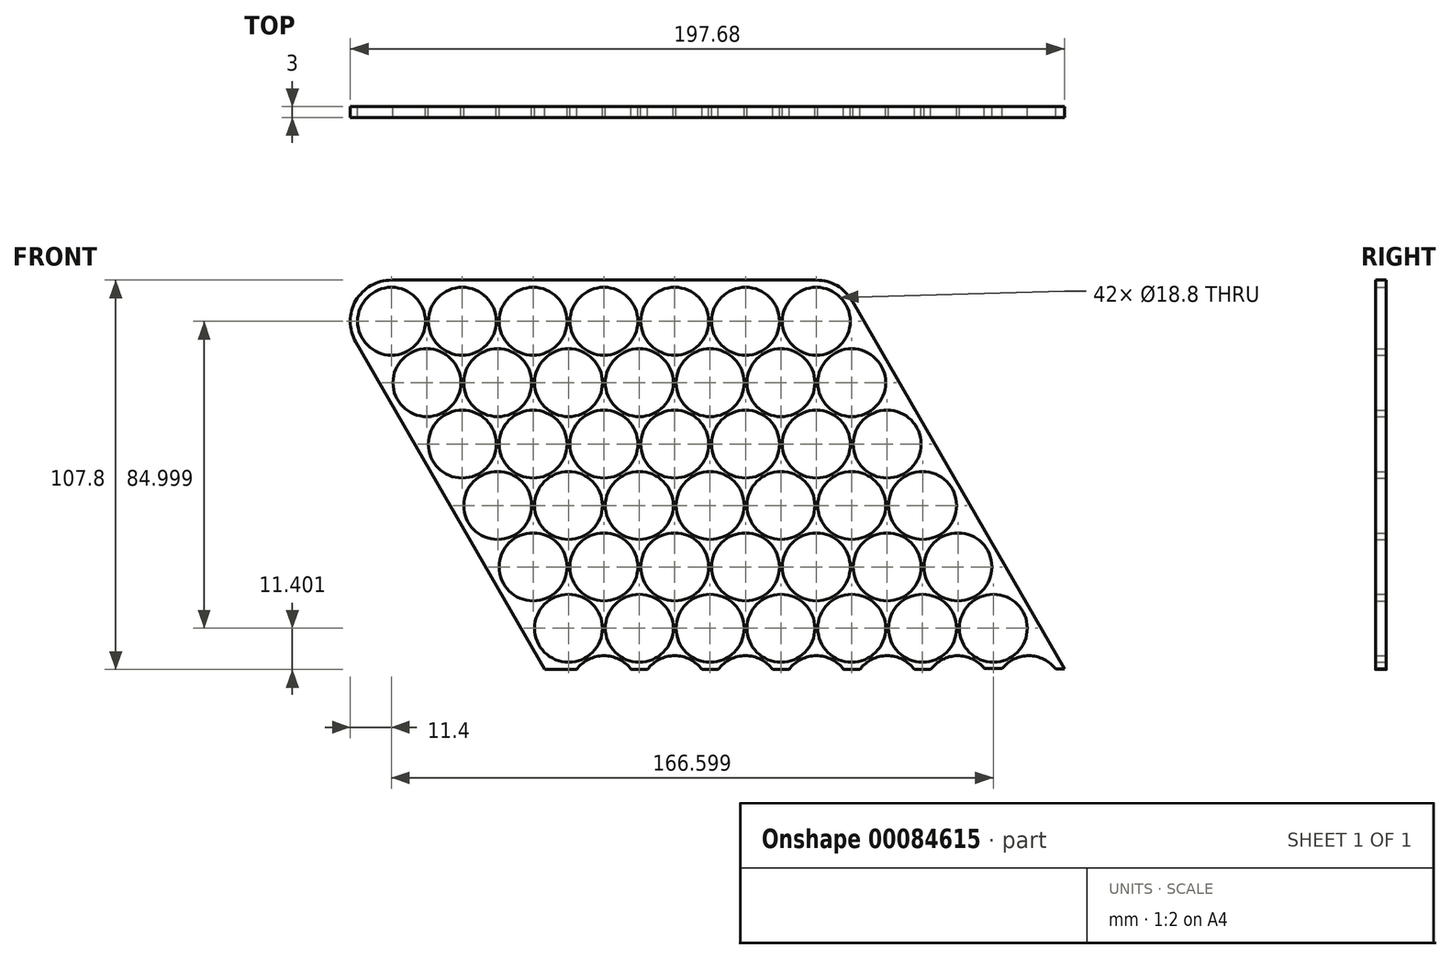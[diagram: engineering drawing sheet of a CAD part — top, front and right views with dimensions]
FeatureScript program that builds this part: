
annotation { "Feature Type Name" : "Feature", "Feature Type Description" : "" }
export const myFeature = defineFeature(function(context is Context, id is Id, definition is map)
    precondition{}
    {
        {
            var Q0;
            Q0=qCreatedBy(makeId("Front.planeOp"),FACE);
            var sketch = newSketch(context, id + "F0", { "sketchPlane" : qUnion([Q0]) });
            skCircle(sketch, "E0", {"center": v(0, 0) * mm, "radius": 9.4 * mm});
            skCircle(sketch, "E1.1.0.0", {"center": v(19.6, 0) * mm, "radius": 9.4 * mm});
            skCircle(sketch, "E1.2.0.0", {"center": v(39.2, 0) * mm, "radius": 9.4 * mm});
            skCircle(sketch, "E1.3.0.0", {"center": v(58.8, 0) * mm, "radius": 9.4 * mm});
            skLineSegment(sketch, "E1.direction1", {"start": v(0, 0) * mm, "end": v(19.6, 0) * mm, "construction": true});
            skLineSegment(sketch, "E2", {"start": v(0, -17) * mm, "end": v(73.2, -17) * mm, "construction": true});
            skLineSegment(sketch, "E3", {"start": v(9.8, 0) * mm, "end": v(9.8, -17) * mm, "construction": true});
            skCircle(sketch, "E4", {"center": v(9.8, -17) * mm, "radius": 9.4 * mm});
            skCircle(sketch, "E5.1.0.0", {"center": v(29.4, -17) * mm, "radius": 9.4 * mm});
            skCircle(sketch, "E5.2.0.0", {"center": v(49, -17) * mm, "radius": 9.4 * mm});
            skCircle(sketch, "E5.3.0.0", {"center": v(68.6, -17) * mm, "radius": 9.4 * mm});
            skLineSegment(sketch, "E5.direction1", {"start": v(9.8, -17) * mm, "end": v(29.4, -17) * mm, "construction": true});
            skLineSegment(sketch, "E6", {"start": v(9.8, -17) * mm, "end": v(9.8, -26.4) * mm, "construction": true});
            skLineSegment(sketch, "E7", {"start": v(68.6, -17) * mm, "end": v(68.6, -26.4) * mm, "construction": true});
            skArc(sketch, "E8", {"start": v(58.8, 9.4) * mm, "mid": v(63.5, 8.14) * mm, "end": v(66.94, 4.7) * mm});
            skArc(sketch, "E9", {"start": v(76.74, -12.3) * mm, "mid": v(76.74, -21.7) * mm, "end": v(68.6, -26.4) * mm});
            skArc(sketch, "E10", {"start": v(9.8, -26.4) * mm, "mid": v(5.1, -25.14) * mm, "end": v(1.66, -21.7) * mm});
            skArc(sketch, "E11", {"start": v(-8.14, -4.7) * mm, "mid": v(-8.14, 4.7) * mm, "end": v(0, 9.4) * mm});
            skArc(sketch, "E12.0", {"start": v(0, 11.4) * mm, "mid": v(-9.87, 5.7) * mm, "end": v(-9.88, -5.7) * mm});
            skLineSegment(sketch, "E13.0", {"start": v(0, 11.4) * mm, "end": v(58.8, 11.4) * mm});
            skLineSegment(sketch, "E14.0", {"start": v(-9.88, -5.7) * mm, "end": v(-0.08, -22.7) * mm});
            skArc(sketch, "E15.trimOffspring", {"start": v(9.8, -5.82) * mm, "mid": v(9.87, -5.71) * mm, "end": v(9.93, -5.6) * mm});
            skArc(sketch, "E16.trimOffspring", {"start": v(9.93, -5.6) * mm, "mid": v(9.86, -5.6) * mm, "end": v(9.8, -5.6) * mm});
            skCircle(sketch, "E17.0.4.0", {"center": v(78.4, 0) * mm, "radius": 9.4 * mm});
            skCircle(sketch, "E17.0.5.0", {"center": v(98, 0) * mm, "radius": 9.4 * mm});
            skCircle(sketch, "E18.0.4.0", {"center": v(88.2, -17) * mm, "radius": 9.4 * mm});
            skCircle(sketch, "E18.0.5.0", {"center": v(107.8, -17) * mm, "radius": 9.4 * mm});
            skLineSegment(sketch, "E19", {"start": v(58.8, 11.4) * mm, "end": v(98, 11.4) * mm});
            skLineSegment(sketch, "E20", {"start": v(0, 0) * mm, "end": v(9.8, -17) * mm, "construction": true});
            skCircle(sketch, "E21.1.0.0", {"center": v(19.6, -34) * mm, "radius": 9.4 * mm});
            skCircle(sketch, "E21.2.0.0", {"center": v(29.4, -51) * mm, "radius": 9.4 * mm});
            skLineSegment(sketch, "E21.direction1", {"start": v(9.8, -17) * mm, "end": v(19.6, -34) * mm, "construction": true});
            skCircle(sketch, "E22.1.0.0", {"center": v(39.2, -34) * mm, "radius": 9.4 * mm});
            skCircle(sketch, "E22.1.0.1", {"center": v(49, -51) * mm, "radius": 9.4 * mm});
            skCircle(sketch, "E22.2.0.0", {"center": v(58.8, -34) * mm, "radius": 9.4 * mm});
            skCircle(sketch, "E22.2.0.1", {"center": v(68.6, -51) * mm, "radius": 9.4 * mm});
            skCircle(sketch, "E22.3.0.0", {"center": v(78.4, -34) * mm, "radius": 9.4 * mm});
            skCircle(sketch, "E22.3.0.1", {"center": v(88.2, -51) * mm, "radius": 9.4 * mm});
            skCircle(sketch, "E22.4.0.0", {"center": v(98, -34) * mm, "radius": 9.4 * mm});
            skCircle(sketch, "E22.4.0.1", {"center": v(107.8, -51) * mm, "radius": 9.4 * mm});
            skCircle(sketch, "E22.5.0.0", {"center": v(117.6, -34) * mm, "radius": 9.4 * mm});
            skCircle(sketch, "E22.5.0.1", {"center": v(127.4, -51) * mm, "radius": 9.4 * mm});
            skLineSegment(sketch, "E22.direction1", {"start": v(19.6, -34) * mm, "end": v(39.2, -34) * mm, "construction": true});
            skLineSegment(sketch, "E23", {"start": v(-0.08, -22.7) * mm, "end": v(19.52, -56.7) * mm});
            skArc(sketch, "E24.0", {"start": v(29.27, -62.4) * mm, "mid": v(29.33, -62.4) * mm, "end": v(29.4, -62.4) * mm});
            skCircle(sketch, "E25.0.6.0", {"center": v(117.6, 0) * mm, "radius": 9.4 * mm});
            skCircle(sketch, "E26.0.6.0", {"center": v(127.4, -17) * mm, "radius": 9.4 * mm});
            skCircle(sketch, "E27.0.6.0", {"center": v(137.2, -34) * mm, "radius": 9.4 * mm});
            skCircle(sketch, "E27.2.6.0", {"center": v(147, -51) * mm, "radius": 9.4 * mm});
            skLineSegment(sketch, "E28", {"start": v(98, 11.4) * mm, "end": v(117.6, 11.4) * mm});
            skCircle(sketch, "E29.0.3.0", {"center": v(39.2, -68) * mm, "radius": 9.4 * mm});
            skCircle(sketch, "E30.1.0.0", {"center": v(58.8, -68) * mm, "radius": 9.4 * mm});
            skCircle(sketch, "E30.2.0.0", {"center": v(78.4, -68) * mm, "radius": 9.4 * mm});
            skCircle(sketch, "E30.3.0.0", {"center": v(98, -68) * mm, "radius": 9.4 * mm});
            skCircle(sketch, "E30.4.0.0", {"center": v(117.6, -68) * mm, "radius": 9.4 * mm});
            skCircle(sketch, "E30.5.0.0", {"center": v(137.2, -68) * mm, "radius": 9.4 * mm});
            skCircle(sketch, "E30.6.0.0", {"center": v(156.8, -68) * mm, "radius": 9.4 * mm});
            skLineSegment(sketch, "E30.direction1", {"start": v(39.2, -68) * mm, "end": v(58.8, -68) * mm, "construction": true});
            skArc(sketch, "E31.0", {"start": v(39.07, -79.4) * mm, "mid": v(39.13, -79.4) * mm, "end": v(39.2, -79.4) * mm});
            skLineSegment(sketch, "E32", {"start": v(19.52, -56.7) * mm, "end": v(29.32, -73.7) * mm});
            skArc(sketch, "E33", {"start": v(127.48, 5.7) * mm, "mid": v(123.3, 9.87) * mm, "end": v(117.6, 11.4) * mm});
            skLineSegment(sketch, "E34", {"start": v(127.48, 5.7) * mm, "end": v(166.68, -62.3) * mm});
            skCircle(sketch, "E35.0.4.0", {"center": v(49, -85) * mm, "radius": 9.4 * mm});
            skArc(sketch, "E35.0.5.0", {"start": v(66.35, -96.4) * mm, "mid": v(58.8, -92.6) * mm, "end": v(51.25, -96.4) * mm});
            skCircle(sketch, "E36.1.0.0", {"center": v(68.6, -85) * mm, "radius": 9.4 * mm});
            skArc(sketch, "E36.1.0.1", {"start": v(85.95, -96.4) * mm, "mid": v(78.4, -92.6) * mm, "end": v(70.85, -96.4) * mm});
            skCircle(sketch, "E36.2.0.0", {"center": v(88.2, -85) * mm, "radius": 9.4 * mm});
            skArc(sketch, "E36.2.0.1", {"start": v(105.55, -96.4) * mm, "mid": v(98, -92.6) * mm, "end": v(90.45, -96.4) * mm});
            skCircle(sketch, "E36.3.0.0", {"center": v(107.8, -85) * mm, "radius": 9.4 * mm});
            skArc(sketch, "E36.3.0.1", {"start": v(125.15, -96.4) * mm, "mid": v(117.6, -92.6) * mm, "end": v(110.05, -96.4) * mm});
            skCircle(sketch, "E36.4.0.0", {"center": v(127.4, -85) * mm, "radius": 9.4 * mm});
            skArc(sketch, "E36.4.0.1", {"start": v(144.75, -96.4) * mm, "mid": v(137.2, -92.6) * mm, "end": v(129.65, -96.4) * mm});
            skCircle(sketch, "E36.5.0.0", {"center": v(147, -85) * mm, "radius": 9.4 * mm});
            skArc(sketch, "E36.5.0.1", {"start": v(164.14, -96.13) * mm, "mid": v(156.63, -92.6) * mm, "end": v(149.25, -96.4) * mm});
            skCircle(sketch, "E36.6.0.0", {"center": v(166.6, -85) * mm, "radius": 9.4 * mm});
            skArc(sketch, "E36.6.0.1", {"start": v(175, -92.7) * mm, "mid": v(171.7, -93.85) * mm, "end": v(169.05, -96.13) * mm});
            skLineSegment(sketch, "E36.direction1", {"start": v(49, -85) * mm, "end": v(68.6, -85) * mm, "construction": true});
            skLineSegment(sketch, "E37", {"start": v(29.32, -73.7) * mm, "end": v(39.12, -90.7) * mm});
            skLineSegment(sketch, "E38", {"start": v(49, -96.4) * mm, "end": v(51.25, -96.4) * mm});
            skLineSegment(sketch, "E39.trimOffspring", {"start": v(66.35, -96.4) * mm, "end": v(70.85, -96.4) * mm});
            skLineSegment(sketch, "E40.trimOffspring", {"start": v(85.95, -96.4) * mm, "end": v(90.45, -96.4) * mm});
            skLineSegment(sketch, "E41.trimOffspring", {"start": v(105.55, -96.4) * mm, "end": v(110.05, -96.4) * mm});
            skLineSegment(sketch, "E42.trimOffspring", {"start": v(125.15, -96.4) * mm, "end": v(129.65, -96.4) * mm});
            skLineSegment(sketch, "E43.trimOffspring", {"start": v(144.75, -96.4) * mm, "end": v(149.25, -96.4) * mm});
            skLineSegment(sketch, "E44.trimOffspring", {"start": v(156.67, -79.4) * mm, "end": v(156.8, -79.4) * mm});
            skLineSegment(sketch, "E45", {"start": v(164.14, -96.13) * mm, "end": v(169.05, -96.13) * mm});
            skLineSegment(sketch, "E46", {"start": v(166.68, -62.3) * mm, "end": v(176.48, -79.3) * mm});
            skArc(sketch, "E47", {"start": v(183.74, -96.13) * mm, "mid": v(176.4, -92.6) * mm, "end": v(169.05, -96.13) * mm});
            skArc(sketch, "E48", {"start": v(183.86, -96.28) * mm, "mid": v(176.5, -92.6) * mm, "end": v(169.05, -96.13) * mm});
            skLineSegment(sketch, "E49", {"start": v(176.48, -79.3) * mm, "end": v(186.28, -96.3) * mm});
            skLineSegment(sketch, "E50", {"start": v(183.86, -96.28) * mm, "end": v(186.28, -96.3) * mm});
            skLineSegment(sketch, "E51", {"start": v(49, -96.4) * mm, "end": v(42.41, -96.4) * mm});
            skLineSegment(sketch, "E52", {"start": v(39.12, -90.7) * mm, "end": v(42.41, -96.4) * mm});
            skSolve(sketch);
        }
        {
            var Q0;
            Q0=qSketchRegion(id+"F0",true);
            var Q1;
            {var subQ3=sQuery(id+"F0.wireOp",EDGE,"E1.1.0.0");Q1=makeQuery(id+"F0.imprint","IMPRINT",FACE,{"disambiguationData":[TD([[makeQuery(id+"F0.imprint","IMPRINT",EDGE,{"derivedFrom":subQ3}),-1.0]])]});}
            extrude(context, id + "F1", {"entities" : qUnion([Q0, Q1]), "depth" : 3 * mm});
        }
    });
